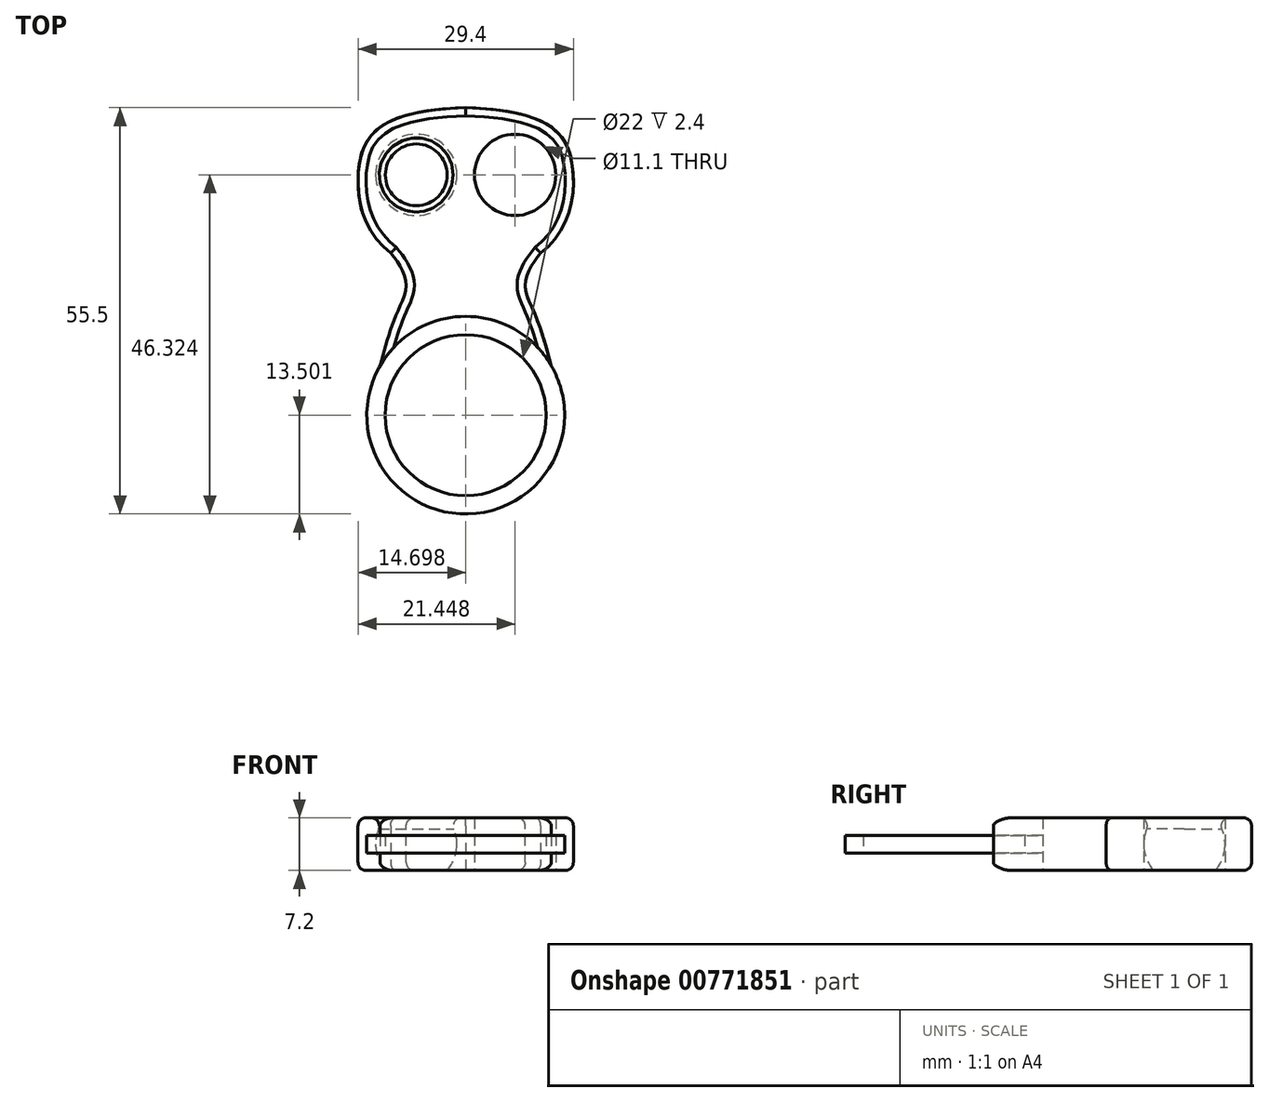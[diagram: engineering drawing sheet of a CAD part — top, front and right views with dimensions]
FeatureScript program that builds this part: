
annotation { "Feature Type Name" : "Feature", "Feature Type Description" : "" }
export const myFeature = defineFeature(function(context is Context, id is Id, definition is map)
    precondition{}
    {
        {
            var Q0;
            Q0=qCreatedBy(makeId("Top.planeOp"),FACE);
            var sketch = newSketch(context, id + "F0", { "sketchPlane" : qUnion([Q0])});
            skCircle(sketch, "E0", {"center": v(0, 0) * mm, "radius": 11 * mm});
            skCircle(sketch, "E1", {"center": v(0, 0) * mm, "radius": 13.5 * mm});
            skLineSegment(sketch, "E2", {"start": v(-60.62, 35) * mm, "end": v(57.4, -33.14) * mm, "construction": true});
            skLineSegment(sketch, "E3.MirrorCS", {"start": v(-60.62, -35) * mm, "end": v(57.4, 33.14) * mm, "construction": true});
            skFitSpline(sketch, "E4", {"points": [v(-11.7, 6.75) * mm, v(-8.5, 16) * mm, v(-10.25, 22.14) * mm], "startDerivative": vector(9.34, 35.35) * mm, "endDerivative": vector(-17.9, 20.96) * mm});
            skLineSegment(sketch, "E5", {"start": v(-61.07, 42) * mm, "end": v(58.93, 42) * mm, "construction": true});
            skFitSpline(sketch, "E6", {"points": [v(-10.25, 22.14) * mm, v(-14.64, 33.32) * mm, v(0, 42) * mm], "startDerivative": vector(-26.2, 21.36) * mm, "endDerivative": vector(68.91, 1.84) * mm});
            skCircle(sketch, "E7", {"center": v(-6.75, 32.82) * mm, "radius": 5.55 * mm});
            skFitSpline(sketch, "E8.MirrorCS", {"points": [v(10.25, 22.14) * mm, v(14.63, 33.32) * mm, v(0, 42) * mm], "startDerivative": vector(26.2, 21.36) * mm, "endDerivative": vector(-68.91, 1.84) * mm});
            skFitSpline(sketch, "E9.MirrorCS", {"points": [v(11.69, 6.75) * mm, v(8.5, 16) * mm, v(10.25, 22.14) * mm], "startDerivative": vector(-9.34, 35.35) * mm, "endDerivative": vector(17.9, 20.96) * mm});
            skCircle(sketch, "E10.MirrorC", {"center": v(6.75, 32.82) * mm, "radius": 5.55 * mm});
            skSolve(sketch);
        }
        {
            var Q0;
            Q0=qCreatedBy(makeId("Top.planeOp"),FACE);
            cPlane(context, id + "F1", {"entities" : qUnion([Q0]), "cplaneType" : CPlaneType.OFFSET, "offset" : 2.4 * mm, "width" : 150 * mm, "height" : 150 * mm});
        }
        {
            var Q0;
            Q0=qCreatedBy(id+"F1.planeOp",FACE);
            var sketch = newSketch(context, id + "F2", { "sketchPlane" : qUnion([Q0])});
            skCircle(sketch, "E11.0", {"center": v(0, 0) * mm, "radius": 13.5 * mm});
            skCircle(sketch, "E11.1", {"center": v(0, 0) * mm, "radius": 11 * mm});
            skSolve(sketch);
        }
        {
            var Q0;
            {var subQ0=sQuery(id+"F0.wireOp",EDGE,"E4");Q0=makeQuery(id+"F0.imprint","IMPRINT",FACE,{"disambiguationData":[TD([[makeQuery(id+"F0.imprint","IMPRINT",EDGE,{"derivedFrom":subQ0}),-1.0]])]});}
            var Q1;
            Q1=makeQuery(id+"F0.imprint","IMPRINT",FACE,{"disambiguationData":[TD([[makeQuery(id+"F0.imprint","IMPRINT",EDGE,{"derivedFrom":sQuery(id+"F0.wireOp",EDGE,"E7")}),1.0]])]});
            var Q2;
            Q2=makeQuery(id+"F0.imprint","IMPRINT",FACE,{"disambiguationData":[TD([[makeQuery(id+"F0.imprint","IMPRINT",EDGE,{"derivedFrom":sQuery(id+"F0.wireOp",EDGE,"E10.MirrorC")}),-1.0]])]});
            extrude(context, id + "F3", {"entities" : qUnion([Q0, Q1, Q2]), "depth" : 7.2 * mm, "offsetDistance" : 25 * mm});
        }
        {
            var Q0;
            Q0=qCreatedBy(makeId("Top.planeOp"),FACE);
            cPlane(context, id + "F4", {"entities" : qUnion([Q0]), "cplaneType" : CPlaneType.OFFSET, "offset" : 3.6 * mm, "width" : 150 * mm, "height" : 150 * mm});
        }
        {
            var Q0;
            Q0=qCreatedBy(id+"F4.planeOp",FACE);
            var sketch = newSketch(context, id + "F5", { "sketchPlane" : qUnion([Q0])});
            skArc(sketch, "E12.0", {"start": v(-1.2, 32.82) * mm, "mid": v(-6.75, 38.37) * mm, "end": v(-12.3, 32.82) * mm});
            skLineSegment(sketch, "E13", {"start": v(-12.3, 32.82) * mm, "end": v(-1.2, 32.82) * mm});
            skArc(sketch, "E14.0", {"start": v(1.2, 32.82) * mm, "mid": v(6.75, 38.37) * mm, "end": v(12.3, 32.82) * mm});
            skLineSegment(sketch, "E15", {"start": v(1.2, 32.82) * mm, "end": v(12.3, 32.82) * mm});
            skSolve(sketch);
        }
        {
            var Q0;
            Q0=qSketchRegion(id+"F5",true);
            var Q1;
            Q1=sQuery(id+"F5.wireOp",EDGE,"E13");
            revolve(context, id + "F6", {"operationType" : NewBodyOperationType.REMOVE, "surfaceOperationType" : NewSurfaceOperationType.NEW, "entities" : qUnion([Q0]), "axis" : qUnion([Q1]), "revolveType" : RevolveType.FULL, "oppositeDirection" : true});
        }
        {
            var Q0;
            Q0=makeQuery(id+"F6.boolean.opBoolean","INTERSECT",EDGE,{"derivedFrom":[makeQuery(id+"F3.opExtrude","CAP_FACE",FACE,{"disambiguationData":[OSD([sQuery(id+"F0.wireOp",EDGE,"E1"),sQuery(id+"F0.wireOp",EDGE,"E4"),sQuery(id+"F0.wireOp",EDGE,"E6"),sQuery(id+"F0.wireOp",EDGE,"E8.MirrorCS"),sQuery(id+"F0.wireOp",EDGE,"E9.MirrorCS")])],"isStart":false}),makeQuery(id+"F6.opRevolve","SWEPT_FACE",FACE,{"disambiguationData":[OSD([sQuery(id+"F5.wireOp",EDGE,"E12.0")])]})]});
            var Q1;
            Q1=makeQuery(id+"F6.boolean.opBoolean","INTERSECT",EDGE,{"derivedFrom":[makeQuery(id+"F3.opExtrude","CAP_FACE",FACE,{"disambiguationData":[OSD([sQuery(id+"F0.wireOp",EDGE,"E1"),sQuery(id+"F0.wireOp",EDGE,"E4"),sQuery(id+"F0.wireOp",EDGE,"E6"),sQuery(id+"F0.wireOp",EDGE,"E8.MirrorCS"),sQuery(id+"F0.wireOp",EDGE,"E9.MirrorCS")])],"isStart":false}),makeQuery(id+"F6.opRevolve","SWEPT_FACE",FACE,{"disambiguationData":[OSD([sQuery(id+"F5.wireOp",EDGE,"E14.0")])]})]});
            fillet(context, id + "F7", {"entities" : qUnion([Q0, Q1]), "radius" : 1.1 * mm, "tangentPropagation" : true, "allowEdgeOverflow" : false});
        }
        {
            var Q0;
            Q0=qSketchRegion(id+"F2",true);
            extrude(context, id + "F8", {"entities" : qUnion([Q0]), "depth" : 2.4 * mm, "offsetDistance" : 25 * mm});
        }
        {
            var Q0;
            Q0=makeQuery(id+"F3.opExtrude","CAP_EDGE",EDGE,{"disambiguationData":[OSD([sQuery(id+"F0.wireOp",EDGE,"E4")])],"isStart":false});
            var Q1;
            Q1=makeQuery(id+"F3.opExtrude","CAP_EDGE",EDGE,{"disambiguationData":[OSD([sQuery(id+"F0.wireOp",EDGE,"E4")])],"isStart":true});
            var Q2;
            Q2=makeQuery(id+"F3.opExtrude","CAP_EDGE",EDGE,{"disambiguationData":[OSD([sQuery(id+"F0.wireOp",EDGE,"E9.MirrorCS")])],"isStart":true});
            var Q3;
            Q3=makeQuery(id+"F3.opExtrude","CAP_EDGE",EDGE,{"disambiguationData":[OSD([sQuery(id+"F0.wireOp",EDGE,"E9.MirrorCS")])],"isStart":false});
            var Q4;
            Q4=makeQuery(id+"F3.opExtrude","CAP_EDGE",EDGE,{"disambiguationData":[OSD([sQuery(id+"F0.wireOp",EDGE,"E8.MirrorCS")])],"isStart":false});
            var Q5;
            Q5=makeQuery(id+"F3.opExtrude","CAP_EDGE",EDGE,{"disambiguationData":[OSD([sQuery(id+"F0.wireOp",EDGE,"E6")])],"isStart":false});
            var Q6;
            Q6=makeQuery(id+"F3.opExtrude","CAP_EDGE",EDGE,{"disambiguationData":[OSD([sQuery(id+"F0.wireOp",EDGE,"E6")])],"isStart":true});
            var Q7;
            Q7=makeQuery(id+"F3.opExtrude","CAP_EDGE",EDGE,{"disambiguationData":[OSD([sQuery(id+"F0.wireOp",EDGE,"E8.MirrorCS")])],"isStart":true});
            fillet(context, id + "F9", {"entities" : qUnion([Q0, Q1, Q2, Q3, Q4, Q5, Q6, Q7]), "radius" : 1.1 * mm, "tangentPropagation" : true, "allowEdgeOverflow" : false});
        }
    });
